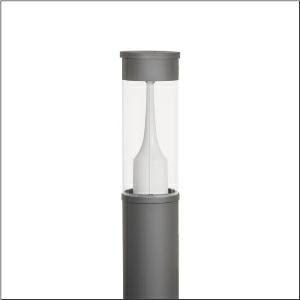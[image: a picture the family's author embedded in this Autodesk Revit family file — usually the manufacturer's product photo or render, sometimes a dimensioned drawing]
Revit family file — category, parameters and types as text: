
# Revit family: city-light_260_iq___p1_0a_5xa5295nf14h_1e18
name_source: partatom
category: Lighting Fixtures
units: mm (PartAtom-declared; Revit-internal decimal feet)

## family parameters
Cut with Voids When Loaded = No
Host = Face
Light Source = No
Part Type = Normal
Room Calculation Point = No
Round Connector Dimension = Use Diameter
Shared = No

## types (1)
- --- (1 x LED, 1510 lm, 11.8 W, 2700K)
    Apparent Load = 12 VA
    CIE Flux Codes = 32 61 90 93 100
    Color Rendering = 70
    Color Temperature = 2700K
    Default Elevation = 1800 mm
    Description = City-Light 260 iQ, light pillar, Module 540 iQ-SR, primary light control with 3 zone facetted reflector, of plastic, silver coated, highly specular, structured, primary optical cover: cover, of PMMA, transparent, partly coated, light distribution: P1.0a, primary light characteristic: strongly asymmetric, LED, High Power LED, rated luminous flux: 1.510lm, luminous efficacy: 128lm/W, light colour: 727, colour temperature: 2700K, control gear: ECG iQ, control: pre-setting: logarithmic dimming characteristic, Street-Remote, Auto-Match, Temp-Guard, Lumen-Switch, Night-Set, Smart-Wire, Light-Fading, Desk-Remote (wireless, voltage-free reading and setting of iQ features in the workshop via application-optimized NFC function/RFID function), optimised constant luminous flux control (CLO 2.0), with terminal, 6-pole, max. 2.5mm², mains connection: 230..240V, AC, 50/60Hz, start of lifetime: 12W, end of service life: 12W, reduction: 6W, luminaire housing, cylindrical, of extruded aluminium section, coated, Siteco® metallic grey (DB 702S), length: 2.600mm, diameter: 200mm, Module 540 iQ-SR, traffic white (RAL 9016), equipment: standard, protection rating (complete): IP65, insulation class (complete): insulation class II (safety insulation), certification: CE, ENEC, VDE, packaging unit: 1 piece

Light Distribution: P1.0a
    Height = 500 mm
    Lamp = 1 x LED
    Lamp Light Flux = 1510 lm
    Lamp Power = 11.8 W
    Lamp count = 1
    Length = 200 mm  [stored 0.656168 ft]
    Luminous efficacy = 128 lm/W
    Manufacturer = Siteco
    ModVariant = No
    Model = 5XA5295NF14H
    Mounting Place = Floor
    Mounting Type = Freestanding
    Number of Poles = 1
    OnlyDefault = Yes
    Power Factor = 1
    Product Name = City-Light 260 iQ | P1.0a
    Product group = light pillar
    ProductGroupID = 1301
    Protection Class = Protection class II
    Protection Degree = IP 65
    RLX_Detail_Level = 1
    RLX_Emergency_Light_Flux = 0 lm
    RLX_Emergency_Type = 0
    RLX_Emergency_Type_DB = No
    RlxData = <blob elided: 52605 chars, md5=88ecefd5>
    Socket = socket
    Standby Power = 0 W
    System Light Flux = 1510 lm
    System Power = 12 W
    Type Comments = factory setting: luminous flux: 100 % | dim-lin: 254 | 472 mA
    Type Image = l_1006918.jpg
    URL = http://relux.com
    VarID = @adj_123523
    Voltage = 0 V
    Weight = 0.00 kg
    Width = 0 mm  [stored 0 ft]

note: [stored X ft] marks values corroborated as IEEE doubles in the binary element streams (Revit-internal decimal feet)

## geometry (parser evidence)
native form markers: Blend x4, Sweep x13
no freeform markers — native parametric forms only
